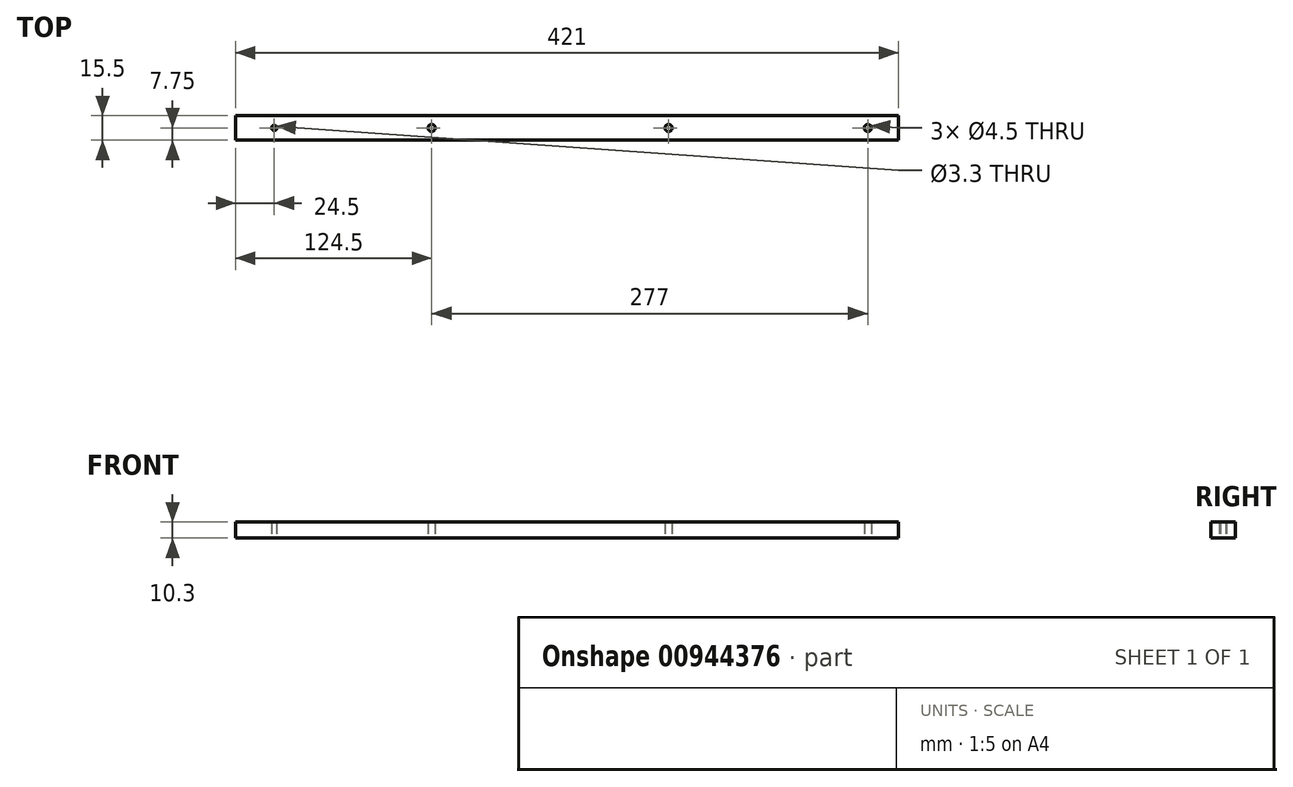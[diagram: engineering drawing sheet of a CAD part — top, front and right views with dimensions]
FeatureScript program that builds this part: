
annotation { "Feature Type Name" : "Feature", "Feature Type Description" : "" }
export const myFeature = defineFeature(function(context is Context, id is Id, definition is map)
    precondition{}
    {
        {
            var Q0;
            Q0=qCreatedBy(makeId("Top.planeOp"),FACE);
            var sketch = newSketch(context, id + "F0", { "sketchPlane" : qUnion([Q0])});
            skLineSegment(sketch, "E0.bottom", {"start": v(-210.5, 7.75) * mm, "end": v(210.5, 7.75) * mm});
            skLineSegment(sketch, "E0.top", {"start": v(-210.5, -7.75) * mm, "end": v(210.5, -7.75) * mm});
            skLineSegment(sketch, "E0.left", {"start": v(-210.5, 7.75) * mm, "end": v(-210.5, -7.75) * mm});
            skLineSegment(sketch, "E0.right", {"start": v(210.5, 7.75) * mm, "end": v(210.5, -7.75) * mm});
            skPoint(sketch, "E0.middle", {"position": v(0, 0) * mm});
            skLineSegment(sketch, "E1", {"start": v(-519.29, 0) * mm, "end": v(537.98, 0) * mm, "construction": true});
            skCircle(sketch, "E2", {"center": v(-186, 0) * mm, "radius": 1.65 * mm});
            skCircle(sketch, "E3", {"center": v(-86, 0) * mm, "radius": 2.25 * mm});
            skCircle(sketch, "E4", {"center": v(64.5, 0) * mm, "radius": 2.25 * mm});
            skCircle(sketch, "E5", {"center": v(191, 0) * mm, "radius": 2.25 * mm});
            skSolve(sketch);
        }
        {
            var Q0;
            Q0=makeQuery(id+"F0.imprint","IMPRINT",FACE,{"disambiguationData":[TD([[makeQuery(id+"F0.imprint","IMPRINT",EDGE,{"derivedFrom":sQuery(id+"F0.wireOp",EDGE,"E0.bottom")}),-1.0]])]});
            extrude(context, id + "F1", {"entities" : qUnion([Q0]), "depth" : 10.3 * mm, "offsetDistance" : 25 * mm});
        }
    });
